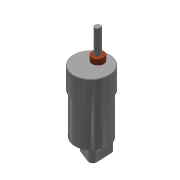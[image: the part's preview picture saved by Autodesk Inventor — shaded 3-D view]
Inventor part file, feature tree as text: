
AUTODESK INVENTOR PART (.ipt)
format: ipt  version: 2016 (Build 200138000, 138)  size: 219,136 bytes
history: native  units: in
note: dims shown in document units (in); Inventor stores cm internally (conversion verified against a paired STEP export)
features: other x4, sketch x4
ambient origin geometry x8: Origin, YZ Plane, XZ Plane, XY Plane, X Axis, Y Axis, Z Axis, Center Point
bodies: Solid1 (feature_tree), Solid2 (feature_tree)
feature tree (8):
  other  "Tetrix motor.ipt"
  other  "DC_MOTOR_2011::Tetrix motor.ipt"
  other  "Solid2::Tetrix motor.ipt"
  other  "TaggingFeature1"
  sketch  "Sketch1"  dims[d0=0.3937in]
  sketch  "Sketch2"  dims[d1=0.5909in d3=0.3436in d5=0.4528in d6=0.4528in d7=0.1654in d8=0.0in d9=0.748in d11=0.4331in d12=0.3661in d13=0.0in d14=0.2165in d16=0.0472in d17=0.0in d18=0.0197in d19=0.0787in d20=0.1181in d21=0.1181in d22=0.5906in d23=0.0in]
  sketch  "Sketch3"
  sketch  "Sketch4"
